# Revit family: Door_Floor-Spring_DORMA_BTS-80
name_source: partatom
category: Türen
revit_build: Autodesk Revit 2016 (Build: 20150220_1215(x64)
units: mm (PartAtom-declared; Revit-internal decimal feet)

## family parameters
Basisbauteil = Fläche
Beim Laden mit Abzugskörper schneiden = Nein
Gemeinsam genutzt = Ja
Raumberechnungspunkt = Nein

## types (3) — shared parameters
Bauelement = P21
Baugruppenkennzeichen = C1020410
Beschreibung = DORMA BTS80 EMB EN4/5/6 electromagnetic hold open universal floor spring
CE mark for building products = Ja
Closing speed adjustable by valve = Ja
Delayed action = Nein
Door closer tested to EN1154 = Ja
Free swing 0-180° = Nein
Handed model: LH (ISO 6) = Ja
Handed model: RH (ISO 5) = Ja
Handed model: universal = Ja
Hersteller = DORMA UK Limited
Hold open, electro-magnetic, hold open point selectable between 75 & 180° = Ja
Hold-open devices tested to EN1155 = Ja
Latching action adjustable at valve = Ja
Material = <Nach Kategorie>
Mechanical backcheck = Ja
Operating voltage in DC +/-15%, residual ripple max. 30% = 24
Power input in Watts = 2.3
Rated for continuous duty = 100
Vorgabe-Ansicht = 1219 mm
Weight in kg = 7.7
_current revision = 1
zero-valued in all types: Barcode, NominalHeight, NominalWidth, SerialNumber, TagNumber, WarrentyDuration

## per-type parameters (varying)
| type | Closing force EN | Fire and smoke check doors upto 1100mm | Fire and smoke check doors upto 1250mm | Fire and smoke check doors upto 1400mm | Standard doors upto 1100mm | Standard doors upto 1250mm | Standard doors upto 1400mm |
| BTS80 EMB EN4 | EN4 | Ja | Nein | Nein | Ja | Nein | Nein |
| BTS80 EMB EN5 | EN5 | Nein | Ja | Nein | Nein | Ja | Nein |
| BTS80 EMB EN6 | EN6 | Nein | Nein | Ja | Nein | Nein | Ja |

note: column(s) folded — value = type name in every type: Modell

## geometry (parser evidence)
native form markers: Blend x4, Sweep x8
no freeform markers — native parametric forms only
